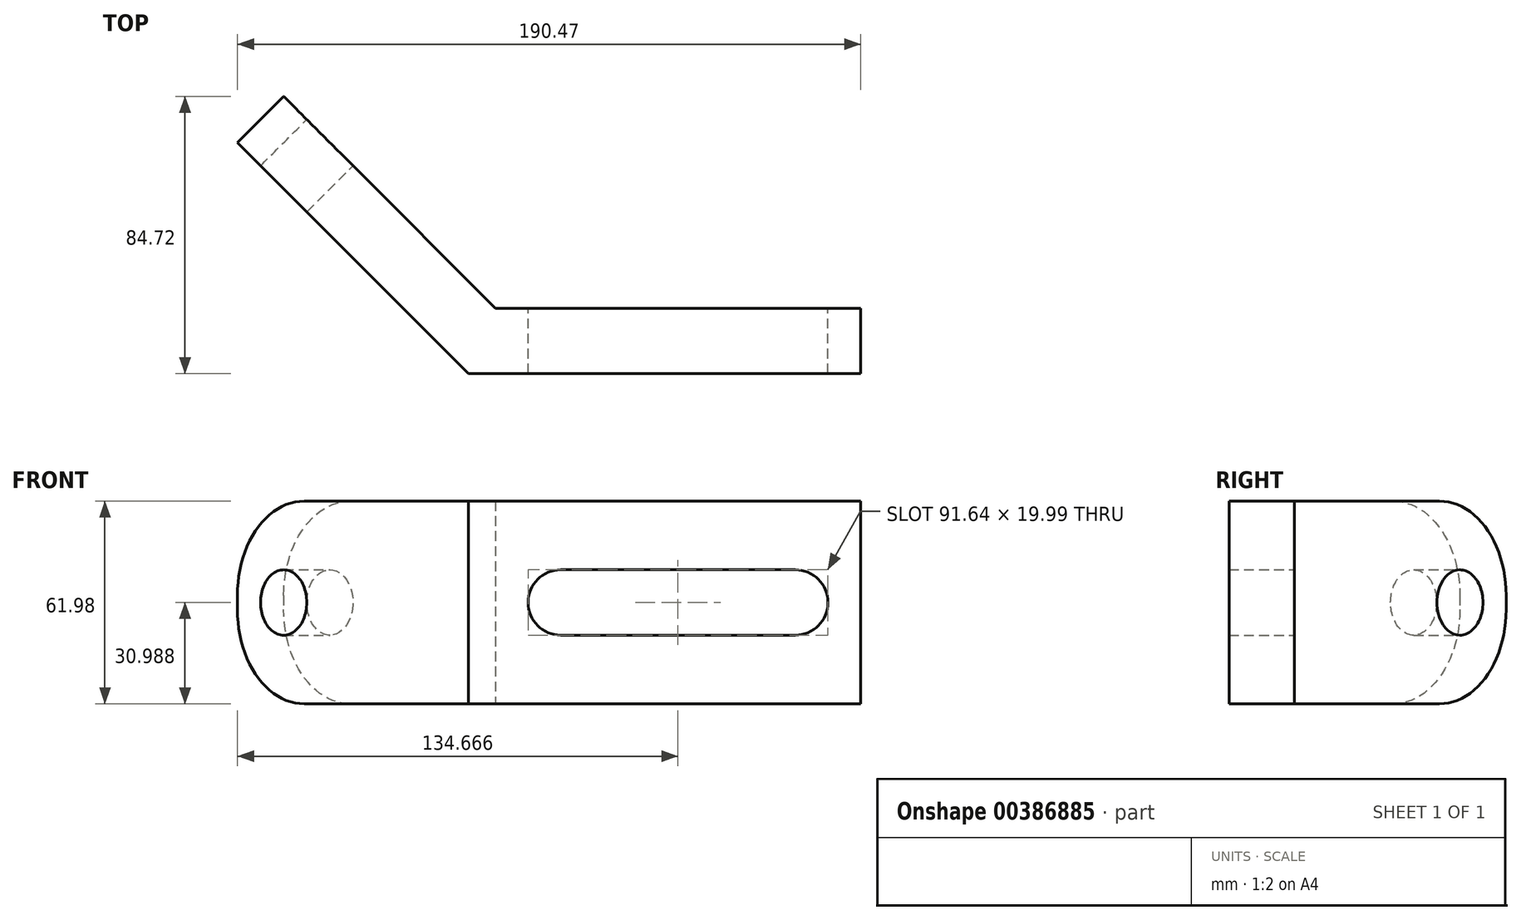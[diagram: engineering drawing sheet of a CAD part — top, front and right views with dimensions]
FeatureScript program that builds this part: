
annotation { "Feature Type Name" : "Feature", "Feature Type Description" : "" }
export const myFeature = defineFeature(function(context is Context, id is Id, definition is map)
    precondition{}
    {
        {
            var Q0;
            Q0=qCreatedBy(makeId("Top.planeOp"),FACE);
            var sketch = newSketch(context, id + "F0", { "sketchPlane" : qUnion([Q0])});
            skLineSegment(sketch, "E0", {"start": v(0, 0) * mm, "end": v(0, 19.99) * mm});
            skLineSegment(sketch, "E1", {"start": v(0, 19.99) * mm, "end": v(-111.6, 19.99) * mm});
            skLineSegment(sketch, "E2", {"start": v(-119.89, 0) * mm, "end": v(0, 0) * mm});
            skLineSegment(sketch, "E3", {"start": v(-119.89, 0) * mm, "end": v(-190.47, 70.58) * mm});
            skLineSegment(sketch, "E4", {"start": v(-190.47, 70.58) * mm, "end": v(-176.34, 84.72) * mm});
            skLineSegment(sketch, "E5", {"start": v(-176.34, 84.72) * mm, "end": v(-111.6, 19.99) * mm});
            skPoint(sketch, "E6.orphan", {"position": v(-119.89, 19.99) * mm});
            skSolve(sketch);
        }
        {
            var Q0;
            Q0 = qSketchRegion(id + "F0", true);
            extrude(context, id + "F1", {"entities" : qUnion([Q0]), "depth" : 61.98 * mm});
        }
        {
            var Q0;
            Q0=makeQuery(id+"F1.opExtrude","SWEPT_FACE",FACE,{"disambiguationData":[OSD([sQuery(id+"F0.wireOp",EDGE,"E1")])]});
            var sketch = newSketch(context, id + "F2", { "sketchPlane" : qUnion([Q0])});
            skArc(sketch, "E7", {"start": v(19.98, 40.98) * mm, "mid": v(9.98, 30.99) * mm, "end": v(19.98, 21) * mm});
            skPoint(sketch, "E7.centerSnap0", {"position": v(0, 30.99) * mm});
            skArc(sketch, "E8", {"start": v(91.63, 21) * mm, "mid": v(101.63, 30.99) * mm, "end": v(91.63, 40.98) * mm});
            skLineSegment(sketch, "E9", {"start": v(19.98, 40.98) * mm, "end": v(91.63, 40.98) * mm});
            skLineSegment(sketch, "E10", {"start": v(19.98, 21) * mm, "end": v(91.63, 21) * mm});
            skSolve(sketch);
        }
        {
            var Q0;
            Q0 = qSketchRegion(id + "F2", true);
            extrude(context, id + "F3", {"entities" : qUnion([Q0]), "operationType" : NewBodyOperationType.REMOVE, "oppositeDirection" : true, "depth" : 35.81 * mm});
        }
        {
            var Q0;
            Q0=makeQuery(id+"F1.opExtrude","SWEPT_FACE",FACE,{"disambiguationData":[OSD([sQuery(id+"F0.wireOp",EDGE,"E5")])]});
            var sketch = newSketch(context, id + "F4", { "sketchPlane" : qUnion([Q0])});
            skCircle(sketch, "E11", {"center": v(164.62, 30.99) * mm, "radius": 10 * mm});
            skPoint(sketch, "E11.centerSnap0", {"position": v(184.6, 30.99) * mm});
            skSolve(sketch);
        }
        {
            var Q0;
            Q0 = qSketchRegion(id + "F4", true);
            extrude(context, id + "F5", {"entities" : qUnion([Q0]), "operationType" : NewBodyOperationType.REMOVE, "oppositeDirection" : true, "depth" : 42.93 * mm});
        }
        {
            var Q0;
            Q0=makeQuery(id+"F1.opExtrude","CAP_EDGE",EDGE,{"disambiguationData":[OSD([sQuery(id+"F0.wireOp",EDGE,"E4")])],"isStart":true});
            var Q1;
            Q1=makeQuery(id+"F1.opExtrude","CAP_EDGE",EDGE,{"disambiguationData":[OSD([sQuery(id+"F0.wireOp",EDGE,"E4")])],"isStart":false});
            fillet(context, id + "F6", {"entities" : qUnion([Q0, Q1]), "radius" : 28.82 * mm, "tangentPropagation" : true, "allowEdgeOverflow" : false});
        }
    });
